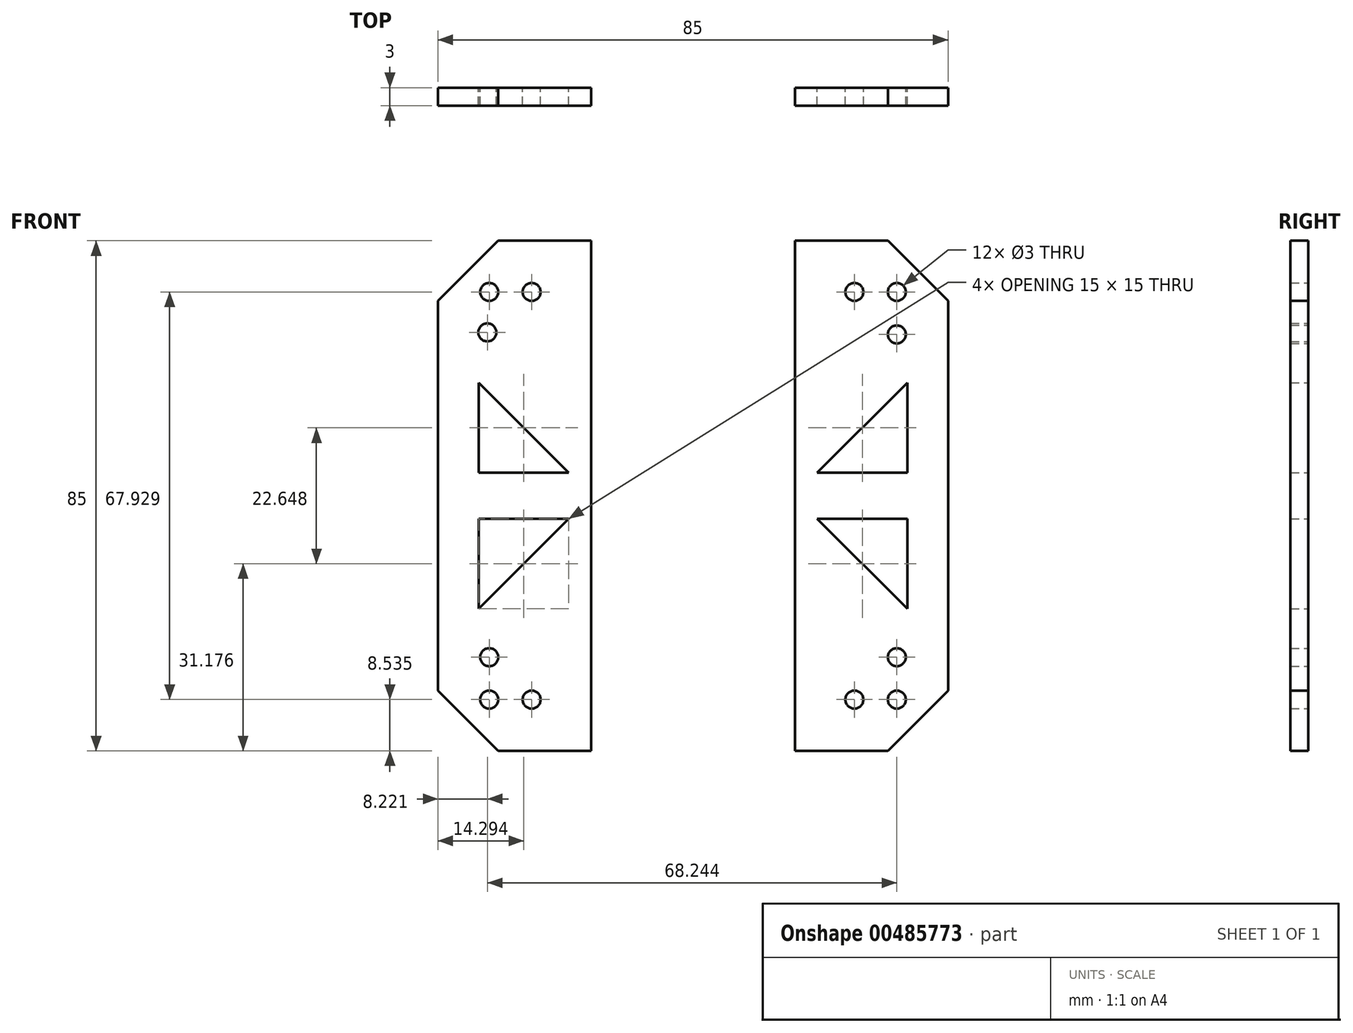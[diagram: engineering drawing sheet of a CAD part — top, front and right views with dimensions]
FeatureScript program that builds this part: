
annotation { "Feature Type Name" : "Feature", "Feature Type Description" : "" }
export const myFeature = defineFeature(function(context is Context, id is Id, definition is map)
    precondition{}
    {
        {
            var Q0;
            Q0=qCreatedBy(makeId("Front.planeOp"),FACE);
            var sketch = newSketch(context, id + "F0", { "sketchPlane" : qUnion([Q0])});
            skLineSegment(sketch, "E0.left", {"start": v(42.5, 42.5) * mm, "end": v(42.5, -42.5) * mm});
            skLineSegment(sketch, "E0.right", {"start": v(-42.5, 42.5) * mm, "end": v(-42.5, -42.5) * mm});
            skPoint(sketch, "E0.middle", {"position": v(0, 0) * mm});
            skLineSegment(sketch, "E1", {"start": v(-42.5, 32.5) * mm, "end": v(-32.5, 42.5) * mm});
            skLineSegment(sketch, "E2", {"start": v(-42.5, 42.5) * mm, "end": v(-30.34, 30.34) * mm});
            skCircle(sketch, "E3", {"center": v(-33.96, 33.96) * mm, "radius": 1.5 * mm});
            skCircle(sketch, "E4", {"center": v(-34.28, 27.22) * mm, "radius": 1.5 * mm});
            skCircle(sketch, "E5", {"center": v(-26.9, 33.96) * mm, "radius": 1.5 * mm});
            skLineSegment(sketch, "E6", {"start": v(-34.28, 27.22) * mm, "end": v(-26.9, 33.96) * mm});
            skLineSegment(sketch, "E7", {"start": v(32.5, 42.5) * mm, "end": v(42.5, 32.5) * mm});
            skLineSegment(sketch, "E8", {"start": v(42.5, 42.5) * mm, "end": v(25.43, 25.43) * mm});
            skCircle(sketch, "E9", {"center": v(33.96, 33.96) * mm, "radius": 1.5 * mm});
            skPoint(sketch, "E9.centerSnap0", {"position": v(33.96, 33.96) * mm});
            skCircle(sketch, "E10", {"center": v(26.9, 33.96) * mm, "radius": 1.5 * mm});
            skCircle(sketch, "E11", {"center": v(33.96, 26.9) * mm, "radius": 1.5 * mm});
            skLineSegment(sketch, "E12", {"start": v(42.5, -32.5) * mm, "end": v(32.5, -42.5) * mm});
            skLineSegment(sketch, "E13", {"start": v(42.5, -42.5) * mm, "end": v(26.16, -26.16) * mm});
            skCircle(sketch, "E14", {"center": v(33.96, -33.96) * mm, "radius": 1.5 * mm});
            skCircle(sketch, "E15", {"center": v(33.96, -26.9) * mm, "radius": 1.5 * mm});
            skCircle(sketch, "E16", {"center": v(26.9, -33.96) * mm, "radius": 1.5 * mm});
            skLineSegment(sketch, "E17", {"start": v(26.9, 33.96) * mm, "end": v(33.96, 26.9) * mm});
            skLineSegment(sketch, "E18", {"start": v(-42.5, -32.5) * mm, "end": v(-32.5, -42.5) * mm});
            skLineSegment(sketch, "E19", {"start": v(-42.5, -42.5) * mm, "end": v(-26, -26) * mm});
            skCircle(sketch, "E20", {"center": v(-33.96, -33.96) * mm, "radius": 1.5 * mm});
            skCircle(sketch, "E21", {"center": v(-26.9, -33.96) * mm, "radius": 1.5 * mm});
            skCircle(sketch, "E22", {"center": v(-33.96, -26.9) * mm, "radius": 1.5 * mm});
            skLineSegment(sketch, "E23", {"start": v(-35.7, 18.82) * mm, "end": v(-35.7, 3.82) * mm});
            skLineSegment(sketch, "E24", {"start": v(-35.7, 3.82) * mm, "end": v(-20.7, 3.82) * mm});
            skLineSegment(sketch, "E25", {"start": v(-20.7, 3.82) * mm, "end": v(-35.7, 18.82) * mm});
            skLineSegment(sketch, "E26.MirrorCS", {"start": v(-35.7, -18.82) * mm, "end": v(-35.7, -3.82) * mm});
            skLineSegment(sketch, "E27.MirrorCS", {"start": v(-20.7, -3.82) * mm, "end": v(-35.7, -18.82) * mm});
            skLineSegment(sketch, "E28.MirrorCS", {"start": v(-35.7, -3.82) * mm, "end": v(-20.7, -3.82) * mm});
            skLineSegment(sketch, "E29.MirrorCS", {"start": v(20.7, 3.82) * mm, "end": v(35.7, 18.82) * mm});
            skLineSegment(sketch, "E30.MirrorCS", {"start": v(35.7, 3.82) * mm, "end": v(20.7, 3.82) * mm});
            skLineSegment(sketch, "E31.MirrorCS", {"start": v(35.7, 18.82) * mm, "end": v(35.7, 3.82) * mm});
            skLineSegment(sketch, "E32.MirrorCS", {"start": v(35.7, -3.82) * mm, "end": v(20.7, -3.82) * mm});
            skLineSegment(sketch, "E33.MirrorCS", {"start": v(20.7, -3.82) * mm, "end": v(35.7, -18.82) * mm});
            skLineSegment(sketch, "E34.MirrorCS", {"start": v(35.7, -18.82) * mm, "end": v(35.7, -3.82) * mm});
            skLineSegment(sketch, "E35", {"start": v(-42.5, 42.5) * mm, "end": v(-17, 42.5) * mm});
            skLineSegment(sketch, "E36", {"start": v(17, 42.5) * mm, "end": v(42.5, 42.5) * mm});
            skLineSegment(sketch, "E37", {"start": v(17, 42.5) * mm, "end": v(17, -42.5) * mm});
            skLineSegment(sketch, "E38", {"start": v(-17, 42.5) * mm, "end": v(-17, -42.5) * mm});
            skLineSegment(sketch, "E39", {"start": v(-42.5, -42.5) * mm, "end": v(-17, -42.5) * mm});
            skLineSegment(sketch, "E40", {"start": v(17, -42.5) * mm, "end": v(42.5, -42.5) * mm});
            skSolve(sketch);
        }
        {
            var Q0;
            Q0=qSketchRegion(id+"F0",true);
            extrude(context, id + "F1", {"entities" : qUnion([Q0]), "depth" : 3 * mm, "offsetDistance" : 25 * mm});
        }
        {
            var Q0;
            Q0=makeQuery(id+"F1.opExtrude","SWEPT_EDGE",EDGE,{"disambiguationData":[OSD([sQuery(id+"F0.wireOp",EDGE,"E0.bottom"),sQuery(id+"F0.wireOp",EDGE,"E0.left")])]});
            var Q1;
            Q1=makeQuery(id+"F1.opExtrude","SWEPT_EDGE",EDGE,{"disambiguationData":[OSD([sQuery(id+"F0.wireOp",EDGE,"E0.bottom"),sQuery(id+"F0.wireOp",EDGE,"E0.right")])]});
            var Q2;
            Q2=makeQuery(id+"F1.opExtrude","SWEPT_EDGE",EDGE,{"disambiguationData":[OSD([sQuery(id+"F0.wireOp",EDGE,"E0.top"),sQuery(id+"F0.wireOp",EDGE,"E0.right")])]});
            var Q3;
            Q3=makeQuery(id+"F1.opExtrude","SWEPT_EDGE",EDGE,{"disambiguationData":[OSD([sQuery(id+"F0.wireOp",EDGE,"E0.top"),sQuery(id+"F0.wireOp",EDGE,"E0.left")])]});
            chamfer(context, id + "F2", {"entities" : qUnion([Q0, Q1, Q2, Q3]), "width" : 10 * mm, "tangentPropagation" : true});
        }
    });
